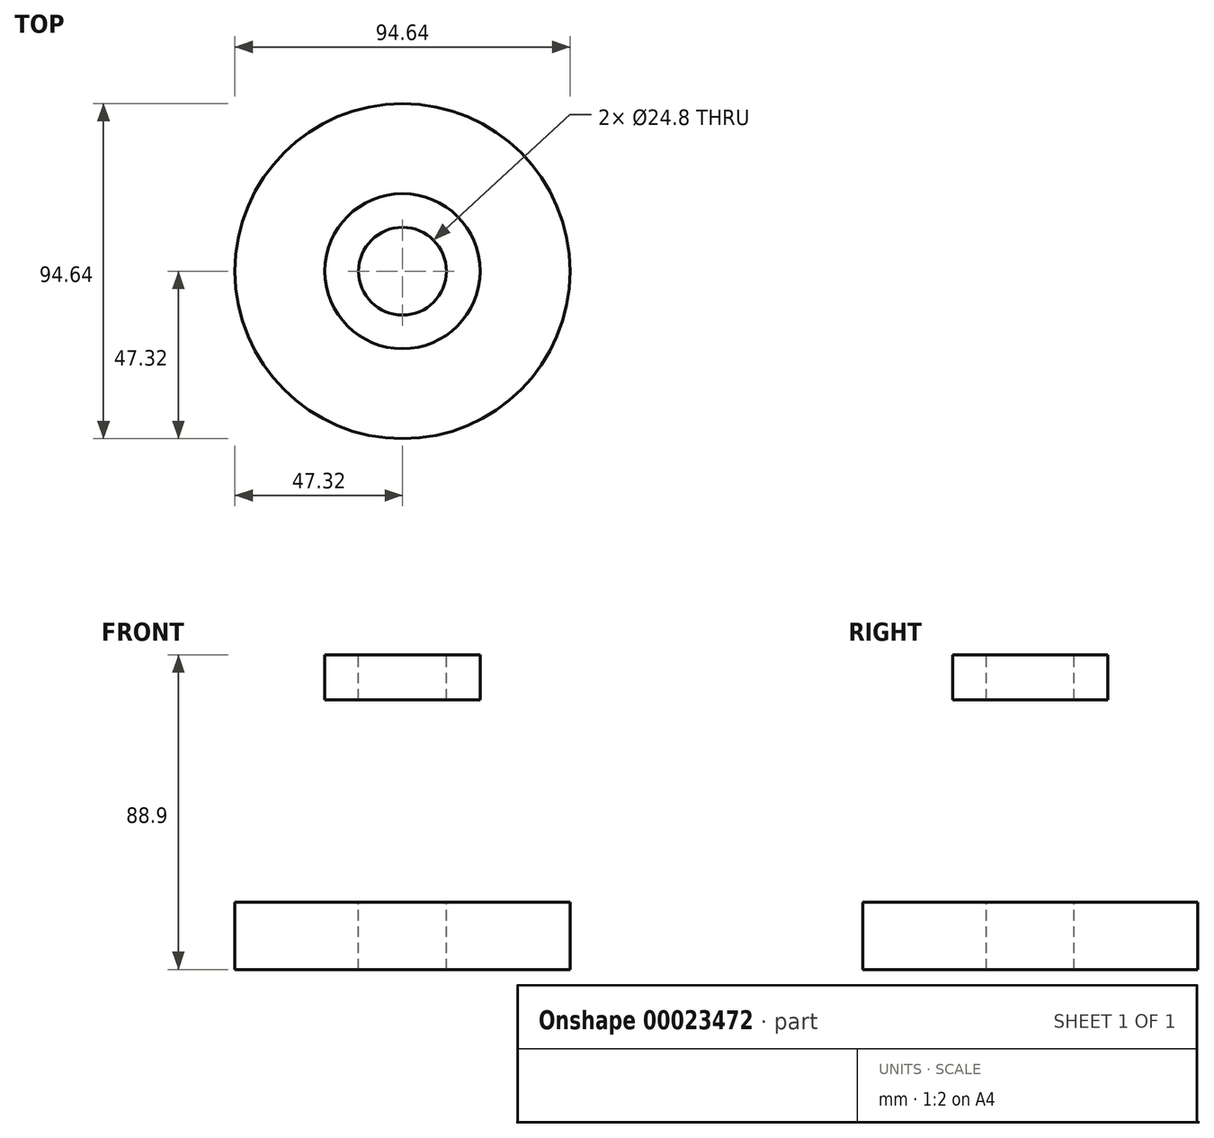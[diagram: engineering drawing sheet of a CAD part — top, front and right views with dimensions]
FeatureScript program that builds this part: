
annotation { "Feature Type Name" : "Feature", "Feature Type Description" : "" }
export const myFeature = defineFeature(function(context is Context, id is Id, definition is map)
    precondition{}
    {
        {
            var Q0;
            Q0=qCreatedBy(makeId("Front.planeOp"),FACE);
            var sketch = newSketch(context, id + "F0", { "sketchPlane" : qUnion([Q0])});
            skLineSegment(sketch, "E0", {"start": v(0, 40.15) * mm, "end": v(0, -49.7) * mm, "construction": true});
            skLineSegment(sketch, "E1", {"start": v(12.4, 40.15) * mm, "end": v(12.4, -49.7) * mm});
            skLineSegment(sketch, "E2", {"start": v(12.4, -49.7) * mm, "end": v(47.32, -49.7) * mm});
            skLineSegment(sketch, "E3", {"start": v(12.4, -30.65) * mm, "end": v(47.32, -30.65) * mm});
            skLineSegment(sketch, "E4", {"start": v(47.32, -30.65) * mm, "end": v(47.32, -49.7) * mm});
            skLineSegment(sketch, "E5.bottom", {"start": v(12.4, -30.65) * mm, "end": v(28.27, -30.65) * mm});
            skLineSegment(sketch, "E5.top", {"start": v(12.4, 26.5) * mm, "end": v(28.27, 26.5) * mm});
            skLineSegment(sketch, "E5.left", {"start": v(12.4, -30.65) * mm, "end": v(12.4, 26.5) * mm});
            skLineSegment(sketch, "E5.right", {"start": v(28.27, -30.65) * mm, "end": v(28.27, 26.5) * mm});
            skLineSegment(sketch, "E6.bottom", {"start": v(12.4, 39.2) * mm, "end": v(21.92, 39.2) * mm});
            skLineSegment(sketch, "E6.top", {"start": v(12.4, 26.5) * mm, "end": v(21.92, 26.5) * mm});
            skLineSegment(sketch, "E6.left", {"start": v(12.4, 39.2) * mm, "end": v(12.4, 26.5) * mm});
            skLineSegment(sketch, "E6.right", {"start": v(21.92, 39.2) * mm, "end": v(21.92, 26.5) * mm});
            skSolve(sketch);
        }
        {
            var Q0;
            Q0=makeQuery(id+"F0.imprint","IMPRINT",FACE,{"disambiguationData":[TD([[makeQuery(id+"F0.imprint","IMPRINT",EDGE,{"derivedFrom":sQuery(id+"F0.wireOp",EDGE,"E6.bottom")}),-1.0]])]});
            var Q1;
            Q1=makeQuery(id+"F0.imprint","IMPRINT",FACE,{"disambiguationData":[TD([[makeQuery(id+"F0.imprint","IMPRINT",EDGE,{"derivedFrom":sQuery(id+"F0.wireOp",EDGE,"E5.bottom")}),1.0]])]});
            var Q2;
            {var subQ1=sQuery(id+"F0.wireOp",EDGE,"E2");Q2=makeQuery(id+"F0.imprint","IMPRINT",FACE,{"disambiguationData":[TD([[makeQuery(id+"F0.imprint","IMPRINT",EDGE,{"derivedFrom":subQ1}),1.0]])]});}
            var Q3;
            Q3=sQuery(id+"F0.wireOp",EDGE,"E0");
            revolve(context, id + "F1", {"entities" : qUnion([Q0, Q1, Q2]), "axis" : qUnion([Q3]), "revolveType" : RevolveType.FULL});
        }
    });
